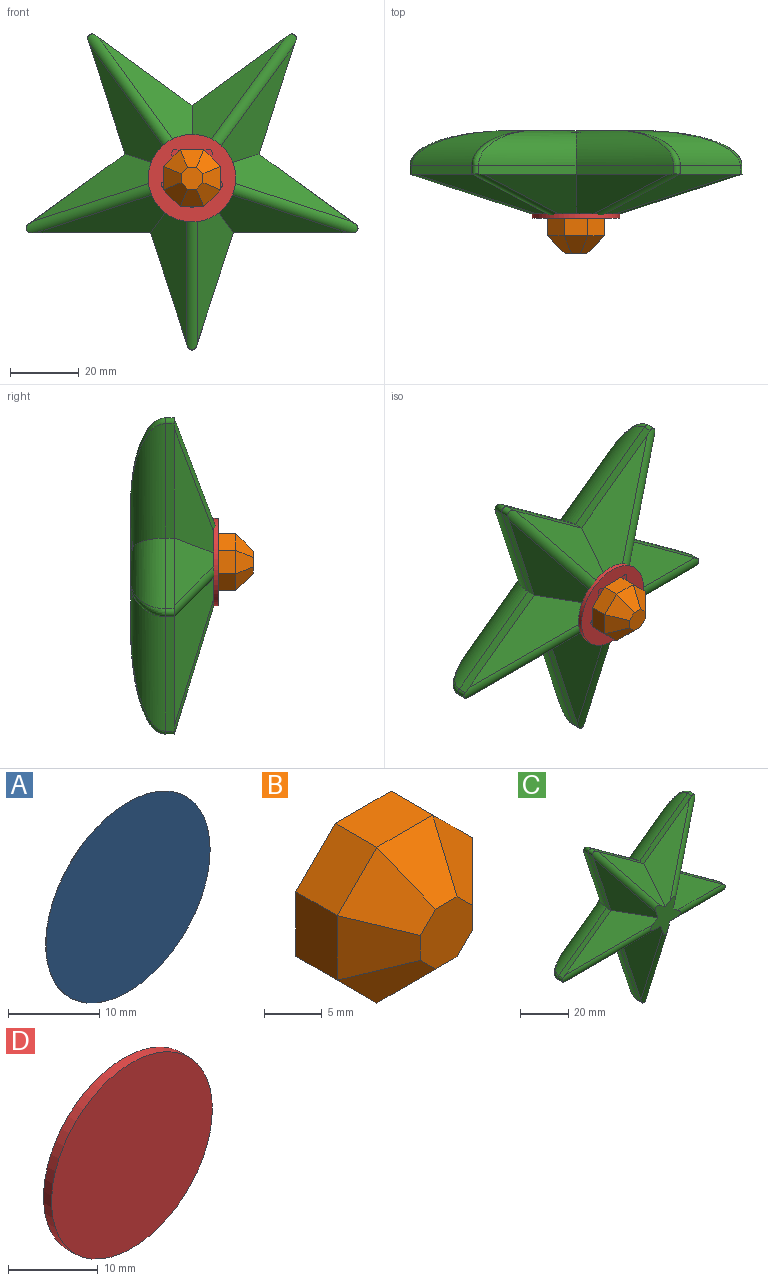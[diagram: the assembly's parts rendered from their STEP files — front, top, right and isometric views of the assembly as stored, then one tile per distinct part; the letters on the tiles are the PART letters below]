
ASSEMBLY  parts=4 mates=3
PART A: 3 faces, bbox 25.4x0x25.4 mm
  f0: cylinder r=12.7mm len=25.4mm, axis (0,1,0), area 2mm2, adj f1,f2
  f1: plane 25.4x25.4mm, normal (0,-1,0), area 506.7mm2, adj f0
  f2: plane 25.4x25.4mm, normal (0,1,0), area 506.7mm2, adj f0
PART B: 18 faces, bbox 16.5x10.2x16.5 mm
  f0: plane 5.08x4.84mm, normal (-0.71,0,0.71), area 34.7mm2, adj f1,f7,f9,f17
  f1: plane 6.84x5.08mm, normal (-1,0,0), area 34.7mm2, adj f0,f2,f9,f15
  f2: plane 5.08x4.84mm, normal (-0.71,0,-0.71), area 34.7mm2, adj f1,f3,f9,f13
  f3: plane 6.84x5.08mm, normal (0,0,-1), area 34.7mm2, adj f2,f4,f9,f11
  f4: plane 5.08x4.84mm, normal (0.71,0,-0.71), area 34.7mm2, adj f3,f5,f9,f10
  f5: plane 6.84x5.08mm, normal (1,0,0), area 34.7mm2, adj f4,f6,f9,f12
  f6: plane 5.08x4.84mm, normal (0.71,0,0.71), area 34.7mm2, adj f5,f7,f9,f14
  f7: plane 6.84x5.08mm, normal (0,0,1), area 34.7mm2, adj f0,f6,f9,f16
  f8: plane 6.35x6.35mm, normal (0,-1,0), area 33.4mm2, adj f10,f11,f12,f13,f14,f15,f16,f17
  f9: plane 16.51x16.51mm, normal (0,1,0), area 225.8mm2, adj f0,f1,f2,f3,f4,f5,f6,f7
  f10: plane 6.94x6.94mm, normal (0.5,-0.71,-0.5), area 34mm2, adj f4,f8,f11,f12
  f11: plane 6.84x5.08mm, normal (0,-0.71,-0.71), area 34mm2, adj f3,f8,f10,f13
  f12: plane 6.84x5.08mm, normal (0.71,-0.71,0), area 34mm2, adj f5,f8,f10,f14
  f13: plane 6.94x6.94mm, normal (-0.5,-0.71,-0.5), area 34mm2, adj f2,f8,f11,f15
  f14: plane 6.94x6.94mm, normal (0.5,-0.71,0.5), area 34mm2, adj f6,f8,f12,f16
  f15: plane 6.84x5.08mm, normal (-0.71,-0.71,0), area 34mm2, adj f1,f8,f13,f17
  f16: plane 6.84x5.08mm, normal (0,-0.71,0.71), area 34mm2, adj f7,f8,f14,f17
  f17: plane 6.94x6.94mm, normal (-0.5,-0.71,0.5), area 34mm2, adj f0,f8,f15,f16
PART C: 47 faces, bbox 101.6x26x96.6 mm
  f0: plane 34.9x2.54mm, normal (0,0,-1), area 88.6mm2, adj f1,f14,f22,f29,f44
  f1: plane 33.19x10.78mm, normal (-0.95,0,-0.31), area 88.6mm2, adj f0,f16,f24,f30,f42
  f2: plane 33.19x10.78mm, normal (0.95,0,-0.31), area 88.6mm2, adj f3,f18,f24,f30,f38
  f3: plane 34.9x2.54mm, normal (0,0,-1), area 88.6mm2, adj f2,f20,f26,f31,f36
  f4: plane 28.23x20.51mm, normal (0.59,0,0.81), area 88.6mm2, adj f5,f21,f26,f31,f32
  f5: plane 33.19x10.78mm, normal (0.95,0,-0.31), area 88.6mm2, adj f4,f19,f23,f28,f33
  f6: plane 28.23x20.51mm, normal (-0.59,0,0.81), area 88.6mm2, adj f7,f17,f23,f28,f37
  f7: plane 28.23x20.51mm, normal (0.59,0,0.81), area 88.6mm2, adj f6,f15,f25,f27,f39
  f8: plane 33.19x10.78mm, normal (-0.95,0,-0.31), area 88.6mm2, adj f9,f13,f25,f27,f43
  f9: plane 28.23x20.51mm, normal (-0.59,0,0.81), area 88.6mm2, adj f8,f12,f22,f29,f45
  f10: plane 17.76x16.97mm, normal (0,-1,0), area 151.6mm2, adj f12,f13,f14,f15,f16,f17,f18,f19
  f11: plane 39.06x37.15mm, normal (0,1,0), area 473.4mm2, adj f32,f33,f36,f37,f38,f39,f42,f43
  f12: plane 41.85x19.56mm, normal (-0.42,-0.71,0.57), area 329.6mm2, adj f9,f10,f13,f29
  f13: plane 36.5x25.21mm, normal (-0.67,-0.71,-0.22), area 329.6mm2, adj f8,f10,f12,f27
  f14: plane 42.51x12.7mm, normal (0,-0.71,-0.71), area 329.6mm2, adj f0,f10,f16,f29
  f15: plane 35.26x26.92mm, normal (0.42,-0.71,0.57), area 329.6mm2, adj f7,f10,f17,f27
  f16: plane 44.35x12.7mm, normal (-0.67,-0.71,-0.22), area 329.6mm2, adj f1,f10,f14,f30
  f17: plane 35.26x26.92mm, normal (-0.42,-0.71,0.57), area 329.6mm2, adj f6,f10,f15,f28
  f18: plane 44.35x12.7mm, normal (0.67,-0.71,-0.22), area 329.6mm2, adj f2,f10,f20,f30
  f19: plane 36.5x25.21mm, normal (0.67,-0.71,-0.22), area 329.6mm2, adj f5,f10,f21,f28
  f20: plane 42.51x12.7mm, normal (0,-0.71,-0.71), area 329.6mm2, adj f3,f10,f18,f31
  f21: plane 41.85x19.56mm, normal (0.42,-0.71,0.57), area 329.6mm2, adj f4,f10,f19,f31
  f22: cylinder r=1.27mm len=2.48mm, axis (0,1,0), area 7.8mm2, adj f0,f9,f29,f46
  f23: cylinder r=1.27mm len=2.48mm, axis (0,1,0), area 7.8mm2, adj f5,f6,f28,f35
  f24: cylinder r=1.27mm len=2.48mm, axis (0,1,0), area 7.8mm2, adj f1,f2,f30,f40
  f25: cylinder r=1.27mm len=2.48mm, axis (0,1,0), area 7.8mm2, adj f7,f8,f27,f41
  f26: cylinder r=1.27mm len=2.48mm, axis (0,1,0), area 7.8mm2, adj f3,f4,f31,f34
  f27: cylinder r=2.54mm len=37.06mm, axis (0.56,-0.3,-0.77), area 162.1mm2, adj f7,f8,f10,f13,f15,f25
  f28: cylinder r=2.54mm len=37.06mm, axis (-0.56,-0.3,-0.77), area 162.1mm2, adj f5,f6,f10,f17,f19,f23
  f29: cylinder r=2.54mm len=42.26mm, axis (-0.91,0.3,-0.3), area 162.1mm2, adj f0,f9,f10,f12,f14,f22
  f30: cylinder r=2.54mm len=43.52mm, axis (0,0.3,-0.96), area 162.1mm2, adj f1,f2,f10,f16,f18,f24
  f31: cylinder r=2.54mm len=42.26mm, axis (0.91,0.3,-0.3), area 162.1mm2, adj f3,f4,f10,f20,f21,f26
  f32: cylinder r=10.16mm len=40.18mm, axis (-0.81,0,0.59), area 441.1mm2, adj f4,f11,f33,f34
  f33: cylinder r=10.16mm len=43.35mm, axis (0.31,0,0.95), area 441.1mm2, adj f5,f11,f32,f35
  f34: bspline ~31.27x12.87mm, area 50.9mm2, adj f26,f32,f36
  f35: bspline ~26.6x19.33mm, area 50.9mm2, adj f23,f33,f37
  f36: cylinder r=10.16mm len=42.28mm, axis (1,0,0), area 441.1mm2, adj f3,f11,f34,f38
  f37: cylinder r=10.16mm len=40.18mm, axis (-0.81,0,-0.59), area 441.1mm2, adj f6,f11,f35,f39
  f38: cylinder r=10.16mm len=43.35mm, axis (0.31,0,0.95), area 441.1mm2, adj f2,f11,f36,f40
  f39: cylinder r=10.16mm len=40.18mm, axis (-0.81,0,0.59), area 441.1mm2, adj f7,f11,f37,f41
  f40: bspline ~32.88x12.87mm, area 50.9mm2, adj f24,f38,f42
  f41: bspline ~26.6x19.33mm, area 50.9mm2, adj f25,f39,f43
  f42: cylinder r=10.16mm len=43.35mm, axis (0.31,0,-0.95), area 441.1mm2, adj f1,f11,f40,f44
  f43: cylinder r=10.16mm len=43.35mm, axis (0.31,0,-0.95), area 441.1mm2, adj f8,f11,f41,f45
  f44: cylinder r=10.16mm len=42.28mm, axis (1,0,0), area 441.1mm2, adj f0,f11,f42,f46
  f45: cylinder r=10.16mm len=40.18mm, axis (-0.81,0,-0.59), area 441.1mm2, adj f9,f11,f43,f46
  f46: bspline ~31.27x12.87mm, area 50.9mm2, adj f22,f44,f45
PART D: 3 faces, bbox 25.4x1.3x25.4 mm
  f0: cylinder r=12.7mm len=25.4mm, axis (0,1,0), area 101.3mm2, adj f1,f2
  f1: plane 25.4x25.4mm, normal (0,-1,0), area 506.7mm2, adj f0
  f2: plane 25.4x25.4mm, normal (0,1,0), area 506.7mm2, adj f0
PLACE A t=(-2.17,24.13,33.2)mm
PLACE B t=(55.21,-0.63,74.84)mm
PLACE C t=(-2.17,24.79,33.2)mm
PLACE D t=(144.69,0.64,45.67)mm
MATE revolute C.f10 <-> D.f0  axis (0,-1,0) through (-2.17,-0.61,32.5)mm
MATE revolute C.f11 <-> A.f0  axis (0,1,0) through (-2.17,24.79,33.2)mm
MATE fastened D.f0 <-> B.f9  axis (0,-1,0) through (-2.17,-0.63,32.5)mm
